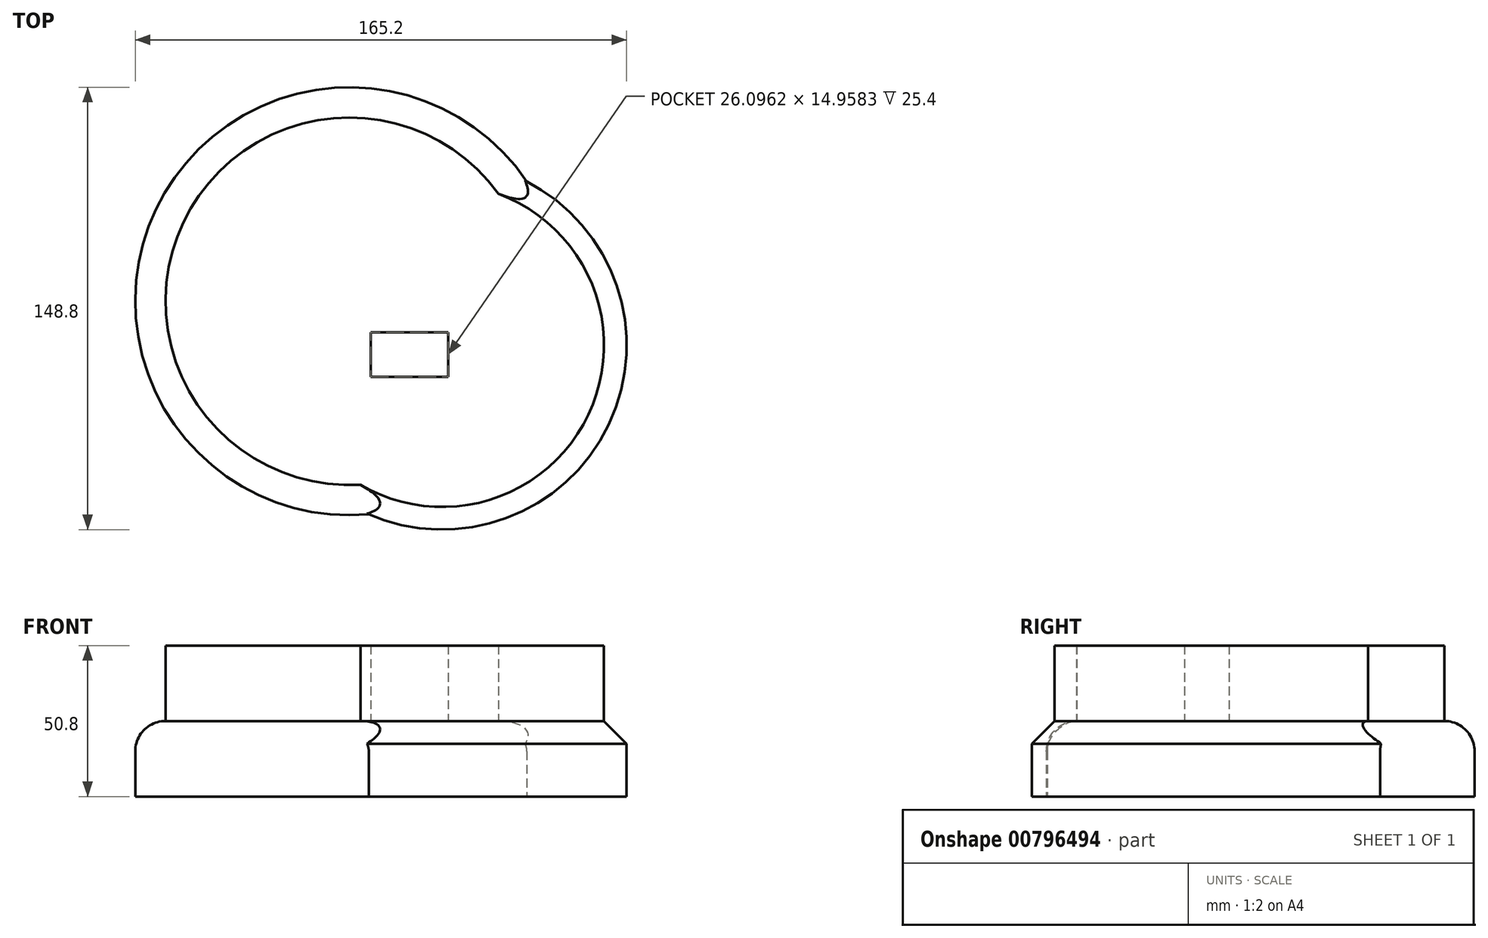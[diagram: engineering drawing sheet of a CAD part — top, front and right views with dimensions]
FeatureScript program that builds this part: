
annotation { "Feature Type Name" : "Feature", "Feature Type Description" : "" }
export const myFeature = defineFeature(function(context is Context, id is Id, definition is map)
    precondition{}
    {
        {
            var Q0;
            Q0=qCreatedBy(makeId("Top.planeOp"),FACE);
            var sketch = newSketch(context, id + "F0", { "sketchPlane" : qUnion([Q0])});
            skCircle(sketch, "E0", {"center": v(0, 0) * mm, "radius": 71.98 * mm});
            skCircle(sketch, "E1", {"center": v(31.24, -14.83) * mm, "radius": 61.99 * mm});
            skSolve(sketch);
        }
        {
            var Q0;
            Q0 = qSketchRegion(id + "F0", true);
            extrude(context, id + "F1", {"entities" : qUnion([Q0]), "depth" : 25.4 * mm, "offsetDistance" : 25.4 * mm});
        }
        {
            var Q0;
            Q0=makeQuery(id+"F1.opExtrude","CAP_EDGE",EDGE,{"disambiguationData":[OSD([sQuery(id+"F0.wireOp",EDGE,"E0")])],"isStart":false});
            fillet(context, id + "F2", {"entities" : qUnion([Q0]), "radius" : 10.16 * mm, "tangentPropagation" : true, "allowEdgeOverflow" : false});
        }
        {
            var Q0;
            Q0=makeQuery(id+"F1.opExtrude","CAP_EDGE",EDGE,{"disambiguationData":[OSD([sQuery(id+"F0.wireOp",EDGE,"E1")])],"isStart":false});
            chamfer(context, id + "F3", {"entities" : qUnion([Q0]), "width" : 7.62 * mm, "tangentPropagation" : true});
        }
        {
            var Q0;
            Q0=makeQuery(id+"F1.opExtrude","CAP_FACE",FACE,{"disambiguationData":[OSD([sQuery(id+"F0.wireOp",EDGE,"E0"),sQuery(id+"F0.wireOp",EDGE,"E1")])],"isStart":false});
            var sketch = newSketch(context, id + "F4", { "sketchPlane" : qUnion([Q0])});
            skLineSegment(sketch, "E2.bottom", {"start": v(33.26, -10.52) * mm, "end": v(7.16, -10.52) * mm});
            skLineSegment(sketch, "E2.top", {"start": v(33.26, -25.48) * mm, "end": v(7.16, -25.48) * mm});
            skLineSegment(sketch, "E2.left", {"start": v(33.26, -10.52) * mm, "end": v(33.26, -25.48) * mm});
            skLineSegment(sketch, "E2.right", {"start": v(7.16, -10.52) * mm, "end": v(7.16, -25.48) * mm});
            skSolve(sketch);
        }
        {
            var Q0;
            Q0=makeQuery(id+"F4.imprint","IMPRINT",FACE,{"disambiguationData":[TD([[makeQuery(id+"F4.imprint","IMPRINT",EDGE,{"derivedFrom":sQuery(id+"F4.wireOp",EDGE,"E2.bottom")}),-1.0]])]});
            extrude(context, id + "F5", {"entities" : qUnion([Q0]), "operationType" : NewBodyOperationType.ADD, "depth" : 25.4 * mm, "offsetDistance" : 25.4 * mm});
        }
    });
